# Revit family: Hager-Univers-IP55-D275-H2050-Cl.II-Steel_encl-CH-it
name_source: partatom
category: Equipement électrique
units: mm (PartAtom-declared; Revit-internal decimal feet)

## family parameters
Configuration du panneau = Deux colonnes, circuits au sein
Cote de connecteur circulaire = Utiliser le diamètre
Couper avec des vides une fois chargée = Non
Hôte = Face
Partagée = Non
Point de calcul de pièce = Non
Type d'élément = Tableau de raccordement

## types (11) — shared parameters
Commentaires du type = Univers
EF000003 - Tipo di montaggio = EV012274 - montaggio a pavimento
EF000007 - colore = EV000270 - grigio
EF000040 - Altezza = 2050 mm  [stored 6.72572 ft]
EF000049 - profondità = 275 mm  [stored 0.902231 ft]
EF000116 - numero RAL = 7035
EF000118 - con piastra di montaggio = Non
EF000266 - numero di file = 12
EF000339 - tipo di copertura = EV004216 - porta
EF001088 - possibilità di applicazione = Oui
EF001131 - profondità interna = 275 mm  [stored 0.902231 ft]
EF001596 - Attacco Lampada = EV000179 - acciaio
EF001613 - Integrità del circuito = EV000494 - senza
EF002950 - Numero moduli DIN = 24
EF003532 - adatto per uso esterno = Non
EF004293 - resistenza agli urti = EV008784 - IK10
EF005474 - grado di protezione (IP) = EV006420 - IP55
EF006306 - con serratura = Non
EF007800 - adatto per parafulmine = Non
EF008873 - corrente nominale (In) = 800 A
EF009170 - spessore materiale scatola = 2 mm  [stored 0.00656168 ft]
EF009171 - spessore materiale porta/coperchio = 2 mm  [stored 0.00656168 ft]
EF009212 - esecuzione coperchio = EV000116 - chiuso
EF015940 - Coprire con rilascio di sovrapressione = Non
Fabricant = Hager
HG000002 - Con porta = Oui
HG000003 - Gamma = Univers
HG000006 - Ad incasso = Non
HG000023 - Custodia a doppia sezione = Non
HG000024 - Altezza della sezione inferiore = 800 mm  [stored 2.62467 ft]
HG000026 - A pavimento = Oui
HG000027 - Altezza dello zoccolo = 200 mm  [stored 0.656168 ft]
zero-valued in all types: EF000218 - profondità di incasso, Elévation par défaut

## per-type parameters (varying)
| type | EF000008 - Larghezza | EF000437 - numero di ingressi per conduttori | EF004427 - numero di moduli | EF004464 - tipo di porta | EF006244 - coperchio/porta trasparente | EF009554 - numero delle aperture per la piastra della flangia | HG000004 - Codice produttore | HG000009 - Porta doppia a battente | HG000010 - Porte asimmetriche |
| montaggio a pavimento IP55 L1050 A2050 P275  - FR24L2 | 1050 mm | 8 | 576 | EV003602 - doppio | Oui | 8 | FR24L2 | Oui | Oui |
| montaggio a pavimento IP55 L1050 A2050 P275  - FR24S2 | 1050 mm | 8 | 576 | EV003602 - doppio | Non | 8 | FR24S2 | Oui | Oui |
| montaggio a pavimento IP55 L1300 A2050 P275  - FR25L2 | 1300 mm  [stored 4.26509 ft] | 10 | 720 | EV003602 - doppio | Oui | 10 | FR25L2 | Oui | Oui |
| montaggio a pavimento IP55 L1300 A2050 P275  - FR25S2 | 1300 mm  [stored 4.26509 ft] | 10 | 720 | EV003602 - doppio | Non | 10 | FR25S2 | Oui | Oui |
| montaggio a pavimento IP55 L1550 A2050 P275  - FR26L2 | 1550 mm  [stored 5.0853 ft] | 12 | 864 | EV003602 - doppio | Oui | 12 | FR26L2 | Oui | Oui |
| montaggio a pavimento IP55 L1550 A2050 P275  - FR26S2 | 1550 mm  [stored 5.0853 ft] | 12 | 864 | EV003602 - doppio | Non | 12 | FR26S2 | Oui | Oui |
| montaggio a pavimento IP55 L300 A2050 P275  - FR21S2 | 300 mm | 2 | 144 | EV002646 - singolo | Non | 2 | FR21S2 | Non | Non |
| montaggio a pavimento IP55 L550 A2050 P275  - FR22L2 | 550 mm | 4 | 288 | EV002646 - singolo | Oui | 4 | FR22L2 | Non | Non |
| montaggio a pavimento IP55 L550 A2050 P275  - FR22S2 | 550 mm | 4 | 288 | EV002646 - singolo | Non | 4 | FR22S2 | Non | Non |
| montaggio a pavimento IP55 L800 A2050 P275  - FR23L2 | 800 mm  [stored 2.62467 ft] | 6 | 432 | EV002646 - singolo | Oui | 6 | FR23L2 | Non | Non |
| montaggio a pavimento IP55 L800 A2050 P275  - FR23S2 | 800 mm  [stored 2.62467 ft] | 6 | 432 | EV002646 - singolo | Non | 6 | FR23S2 | Non | Non |

note: [stored X ft] marks values corroborated as IEEE doubles in the binary element streams (Revit-internal decimal feet)

## geometry (parser evidence)
native form markers: Sweep x10
no freeform markers — native parametric forms only
